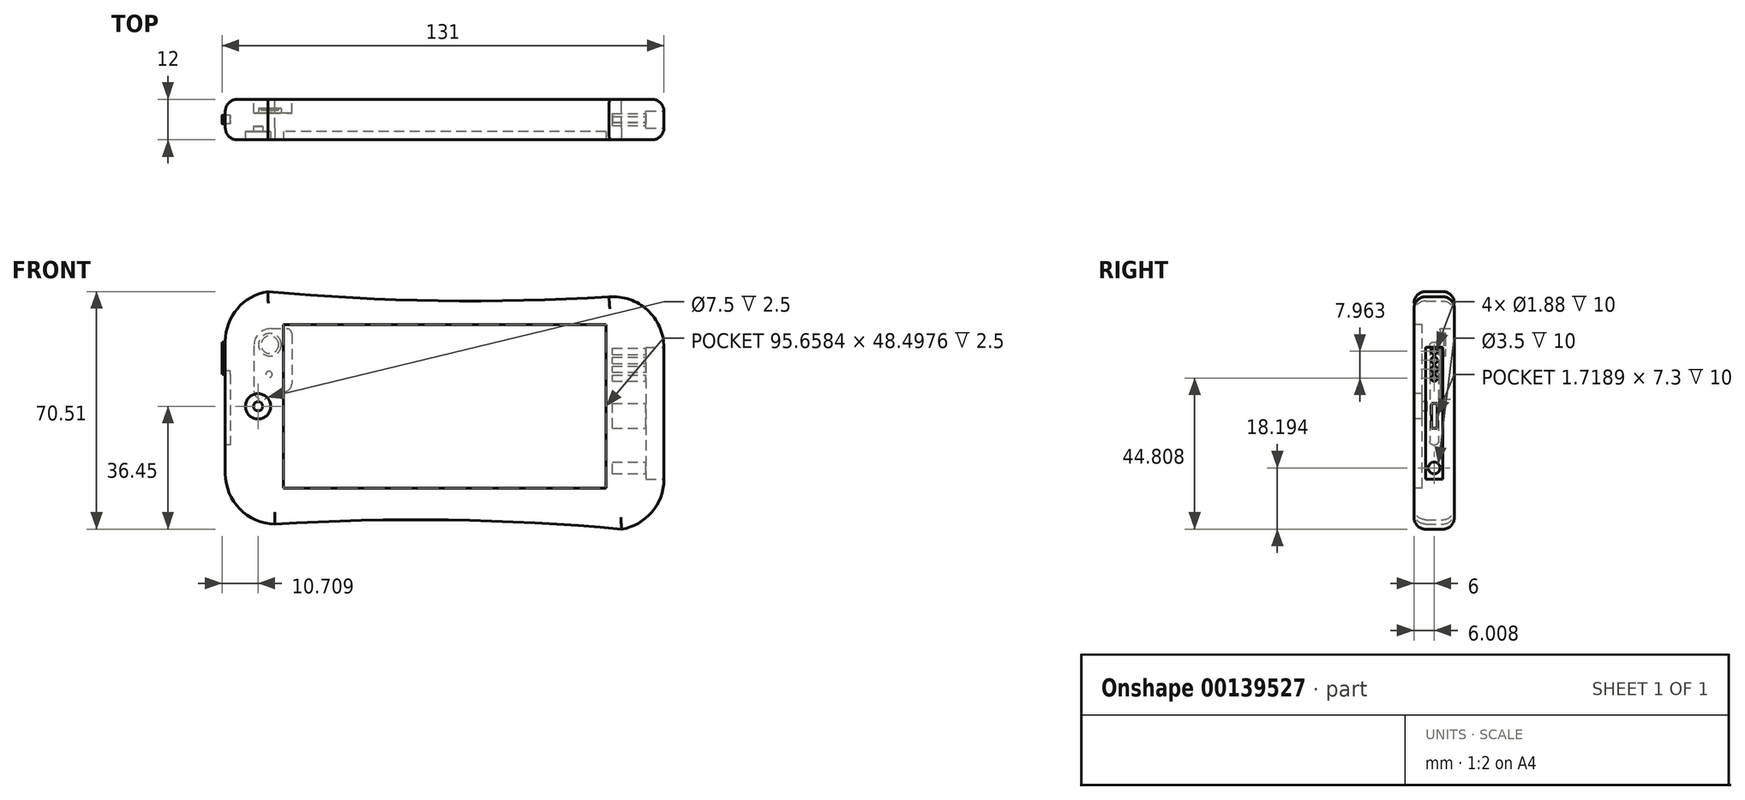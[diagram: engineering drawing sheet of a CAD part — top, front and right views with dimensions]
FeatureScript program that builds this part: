
annotation { "Feature Type Name" : "Feature", "Feature Type Description" : "" }
export const myFeature = defineFeature(function(context is Context, id is Id, definition is map)
    precondition{}
    {
        {
            var Q0;
            Q0=qCreatedBy(makeId("Front.planeOp"),FACE);
            var sketch = newSketch(context, id + "F0", { "sketchPlane" : qUnion([Q0])});
            skLineSegment(sketch, "E0.left", {"start": v(65, 17.5) * mm, "end": v(65, -21.65) * mm});
            skLineSegment(sketch, "E0.right", {"start": v(-65, 19.26) * mm, "end": v(-65, -19.94) * mm});
            skPoint(sketch, "E0.middle", {"position": v(0, 0) * mm});
            skPoint(sketch, "E1.visualSharp", {"position": v(-65, 3) * mm});
            skArc(sketch, "E1.filletArc", {"start": v(-52.42, 34.06) * mm, "mid": v(-61.43, 28.97) * mm, "end": v(-65, 19.26) * mm});
            skPoint(sketch, "E2.visualSharp", {"position": v(-65, -65) * mm});
            skArc(sketch, "E2.filletArc", {"start": v(-65, -19.94) * mm, "mid": v(-60.72, -30.44) * mm, "end": v(-50.32, -34.94) * mm});
            skPoint(sketch, "E3.visualSharp", {"position": v(65, 65) * mm});
            skArc(sketch, "E3.filletArc", {"start": v(65, 17.5) * mm, "mid": v(60.14, 28.56) * mm, "end": v(48.7, 32.45) * mm});
            skPoint(sketch, "E4.visualSharp", {"position": v(65, -3) * mm});
            skArc(sketch, "E4.filletArc", {"start": v(52.42, -36.45) * mm, "mid": v(61.43, -31.36) * mm, "end": v(65, -21.65) * mm});
            skArc(sketch, "E5", {"start": v(-52.42, 34.06) * mm, "mid": v(-1.89, 31.33) * mm, "end": v(48.7, 32.45) * mm});
            skArc(sketch, "E6", {"start": v(52.42, -36.45) * mm, "mid": v(1.07, -33.71) * mm, "end": v(-50.32, -34.94) * mm});
            skPoint(sketch, "E7", {"position": v(-45, 23.39) * mm});
            skPoint(sketch, "E8", {"position": v(45, 22.22) * mm});
            skPoint(sketch, "E9", {"position": v(45, -25.78) * mm});
            skPoint(sketch, "E10", {"position": v(-45, -24.61) * mm});
            skLineSegment(sketch, "E11", {"start": v(-45, 23.39) * mm, "end": v(-45, -24.61) * mm});
            skLineSegment(sketch, "E12", {"start": v(45, -25.78) * mm, "end": v(-45, -24.61) * mm});
            skLineSegment(sketch, "E13", {"start": v(45, -25.78) * mm, "end": v(45, 22.22) * mm});
            skLineSegment(sketch, "E14", {"start": v(45, 22.22) * mm, "end": v(-45, 23.39) * mm});
            skSolve(sketch);
        }
        {
            var Q0;
            Q0=makeQuery(id+"F0.imprint","IMPRINT",FACE,{"disambiguationData":[TD([[makeQuery(id+"F0.imprint","IMPRINT",EDGE,{"derivedFrom":sQuery(id+"F0.wireOp",EDGE,"E11")}),1.0]])]});
            var Q1;
            Q1=makeQuery(id+"F0.imprint","IMPRINT",FACE,{"disambiguationData":[TD([[makeQuery(id+"F0.imprint","IMPRINT",EDGE,{"derivedFrom":sQuery(id+"F0.wireOp",EDGE,"E0.left")}),-1.0]])]});
            extrude(context, id + "F1", {"entities" : qUnion([Q0, Q1]), "depth" : 12 * mm});
        }
        {
            var Q0;
            Q0=makeQuery(id+"F1.opExtrude","CAP_FACE",FACE,{"disambiguationData":[OSD([sQuery(id+"F0.wireOp",EDGE,"E0.left"),sQuery(id+"F0.wireOp",EDGE,"E0.right"),sQuery(id+"F0.wireOp",EDGE,"E1.filletArc"),sQuery(id+"F0.wireOp",EDGE,"E2.filletArc"),sQuery(id+"F0.wireOp",EDGE,"E3.filletArc"),sQuery(id+"F0.wireOp",EDGE,"E4.filletArc"),sQuery(id+"F0.wireOp",EDGE,"E5"),sQuery(id+"F0.wireOp",EDGE,"E6")])],"isStart":false});
            fillet(context, id + "F2", {"entities" : qUnion([Q0]), "radius" : 3.5 * mm, "tangentPropagation" : true, "allowEdgeOverflow" : false});
        }
        {
            var Q0;
            Q0=makeQuery(id+"F1.opExtrude","CAP_FACE",FACE,{"disambiguationData":[OSD([sQuery(id+"F0.wireOp",EDGE,"E0.left"),sQuery(id+"F0.wireOp",EDGE,"E0.right"),sQuery(id+"F0.wireOp",EDGE,"E1.filletArc"),sQuery(id+"F0.wireOp",EDGE,"E2.filletArc"),sQuery(id+"F0.wireOp",EDGE,"E3.filletArc"),sQuery(id+"F0.wireOp",EDGE,"E4.filletArc"),sQuery(id+"F0.wireOp",EDGE,"E5"),sQuery(id+"F0.wireOp",EDGE,"E6")])],"isStart":true});
            fillet(context, id + "F3", {"entities" : qUnion([Q0]), "radius" : 3.5 * mm, "tangentPropagation" : true, "allowEdgeOverflow" : false});
        }
        {
            var Q0;
            Q0=makeQuery(id+"F1.opExtrude","CAP_FACE",FACE,{"disambiguationData":[OSD([sQuery(id+"F0.wireOp",EDGE,"E0.left"),sQuery(id+"F0.wireOp",EDGE,"E0.right"),sQuery(id+"F0.wireOp",EDGE,"E1.filletArc"),sQuery(id+"F0.wireOp",EDGE,"E2.filletArc"),sQuery(id+"F0.wireOp",EDGE,"E3.filletArc"),sQuery(id+"F0.wireOp",EDGE,"E4.filletArc"),sQuery(id+"F0.wireOp",EDGE,"E5"),sQuery(id+"F0.wireOp",EDGE,"E6")])],"isStart":false});
            var sketch = newSketch(context, id + "F4", { "sketchPlane" : qUnion([Q0])});
            skLineSegment(sketch, "E15.bottom", {"start": v(47.83, -24.25) * mm, "end": v(-47.83, -24.25) * mm});
            skLineSegment(sketch, "E15.top", {"start": v(47.83, 24.25) * mm, "end": v(-47.83, 24.25) * mm});
            skLineSegment(sketch, "E15.left", {"start": v(47.83, -24.25) * mm, "end": v(47.83, 24.25) * mm});
            skLineSegment(sketch, "E15.right", {"start": v(-47.83, -24.25) * mm, "end": v(-47.83, 24.25) * mm});
            skPoint(sketch, "E15.middle", {"position": v(0, 0) * mm});
            skCircle(sketch, "E16", {"center": v(-55.3, 0) * mm, "radius": 3.75 * mm});
            skSolve(sketch);
        }
        {
            var Q0;
            Q0 = qSketchRegion(id + "F4", true);
            extrude(context, id + "F5", {"entities" : qUnion([Q0]), "operationType" : NewBodyOperationType.REMOVE, "oppositeDirection" : true, "depth" : 2.5 * mm});
        }
        {
            var Q0;
            Q0=makeQuery(id+"F5.boolean.opBoolean","COPY",FACE,{"derivedFrom":makeQuery(id+"F5.opExtrude","CAP_FACE",FACE,{"disambiguationData":[OSD([sQuery(id+"F4.wireOp",EDGE,"E16")])],"isStart":false})});
            var sketch = newSketch(context, id + "F6", { "sketchPlane" : qUnion([Q0])});
            skCircle(sketch, "E17", {"center": v(-55.3, 0) * mm, "radius": 1.37 * mm});
            skSolve(sketch);
        }
        {
            var Q0;
            Q0 = qSketchRegion(id + "F6", true);
            extrude(context, id + "F7", {"entities" : qUnion([Q0]), "operationType" : NewBodyOperationType.REMOVE, "oppositeDirection" : true, "depth" : 1.5 * mm});
        }
        {
            var Q0;
            Q0=makeQuery(id+"F1.opExtrude","SWEPT_FACE",FACE,{"disambiguationData":[OSD([sQuery(id+"F0.wireOp",EDGE,"E0.left")])]});
            var sketch = newSketch(context, id + "F8", { "sketchPlane" : qUnion([Q0])});
            skSolve(sketch);
        }
        {
            var Q0;
            {var subQ0=sQuery(id+"F0.wireOp",EDGE,"E0.left");var subQ1=makeQuery(id+"F1.opExtrude","SWEPT_FACE",FACE,{"disambiguationData":[OSD([subQ0])]});Q0=makeQuery(id+"F8.imprint","IMPRINT",FACE,{"disambiguationData":[TD([[makeQuery(id+"F8.imprint","IMPRINT",EDGE,{"derivedFrom":makeQuery(id+"F2.opFillet","BLEND_EDGE",EDGE,{"blendedFrom":[makeQuery(id+"F1.opExtrude","CAP_EDGE",EDGE,{"disambiguationData":[OSD([subQ0])],"isStart":false}),subQ1],"blendedInto":[subQ1]})}),1.0]])]});}
            extrude(context, id + "F9", {"entities" : qUnion([Q0]), "operationType" : NewBodyOperationType.REMOVE, "oppositeDirection" : true, "depth" : 5.3 * mm});
        }
        {
            var Q0;
            Q0=makeQuery(id+"F9.boolean.opBoolean","COPY",FACE,{"derivedFrom":makeQuery(id+"F9.opExtrude","CAP_FACE",FACE,{"disambiguationData":[OSD([sQuery(id+"F0.wireOp",EDGE,"E0.left"),sQuery(id+"F0.wireOp",EDGE,"E3.filletArc"),sQuery(id+"F0.wireOp",EDGE,"E4.filletArc")])],"isStart":false})});
            var sketch = newSketch(context, id + "F10", { "sketchPlane" : qUnion([Q0])});
            skCircle(sketch, "E18", {"center": v(-6, -18.25) * mm, "radius": 1.75 * mm});
            skPoint(sketch, "E18.centerSnap0", {"position": v(-6, -21.65) * mm});
            skLineSegment(sketch, "E19.bottom", {"start": v(-6.77, -6.49) * mm, "end": v(-5.05, -6.49) * mm});
            skLineSegment(sketch, "E19.top", {"start": v(-6.77, 0.81) * mm, "end": v(-5.05, 0.81) * mm});
            skLineSegment(sketch, "E19.left", {"start": v(-6.77, -6.49) * mm, "end": v(-6.77, 0.81) * mm});
            skLineSegment(sketch, "E19.right", {"start": v(-5.05, -6.49) * mm, "end": v(-5.05, 0.81) * mm});
            skCircle(sketch, "E20", {"center": v(-6, 8.36) * mm, "radius": 0.94 * mm});
            skCircle(sketch, "E21.0.1.0", {"center": v(-6, 11.01) * mm, "radius": 0.94 * mm});
            skCircle(sketch, "E21.0.2.0", {"center": v(-6, 13.67) * mm, "radius": 0.94 * mm});
            skCircle(sketch, "E21.0.3.0", {"center": v(-6, 16.32) * mm, "radius": 0.94 * mm});
            skLineSegment(sketch, "E21.direction1", {"start": v(-6, 8.36) * mm, "end": v(19, 8.36) * mm, "construction": true});
            skLineSegment(sketch, "E21.direction2", {"start": v(-6, 8.36) * mm, "end": v(-6, 11.01) * mm, "construction": true});
            skSolve(sketch);
        }
        {
            var Q0;
            Q0 = qSketchRegion(id + "F10", true);
            extrude(context, id + "F11", {"entities" : qUnion([Q0]), "operationType" : NewBodyOperationType.REMOVE, "oppositeDirection" : true, "depth" : 10 * mm});
        }
        {
            var Q0;
            Q0=makeQuery(id+"F1.opExtrude","CAP_FACE",FACE,{"disambiguationData":[OSD([sQuery(id+"F0.wireOp",EDGE,"E0.left"),sQuery(id+"F0.wireOp",EDGE,"E0.right"),sQuery(id+"F0.wireOp",EDGE,"E1.filletArc"),sQuery(id+"F0.wireOp",EDGE,"E2.filletArc"),sQuery(id+"F0.wireOp",EDGE,"E3.filletArc"),sQuery(id+"F0.wireOp",EDGE,"E4.filletArc"),sQuery(id+"F0.wireOp",EDGE,"E5"),sQuery(id+"F0.wireOp",EDGE,"E6")])],"isStart":true});
            var sketch = newSketch(context, id + "F12", { "sketchPlane" : qUnion([Q0])});
            skLineSegment(sketch, "E22.bottom", {"start": v(51.5, 23.03) * mm, "end": v(46.78, 23.03) * mm});
            skLineSegment(sketch, "E22.left", {"start": v(56.5, 18.03) * mm, "end": v(56.5, 4.58) * mm});
            skLineSegment(sketch, "E22.right", {"start": v(45.28, 21.53) * mm, "end": v(45.28, 6.8) * mm});
            skLineSegment(sketch, "E23", {"start": v(46.94, 4.44) * mm, "end": v(53.16, 2.22) * mm});
            skPoint(sketch, "E24.visualSharp", {"position": v(45.28, 5.03) * mm});
            skArc(sketch, "E24.filletArc", {"start": v(45.28, 6.8) * mm, "mid": v(45.74, 5.35) * mm, "end": v(46.94, 4.44) * mm});
            skPoint(sketch, "E25.visualSharp", {"position": v(56.5, 1.03) * mm});
            skArc(sketch, "E25.filletArc", {"start": v(53.16, 2.22) * mm, "mid": v(55.44, 2.53) * mm, "end": v(56.5, 4.58) * mm});
            skPoint(sketch, "E26.visualSharp", {"position": v(56.5, 23.03) * mm});
            skArc(sketch, "E26.filletArc", {"start": v(56.5, 18.03) * mm, "mid": v(55.03, 21.57) * mm, "end": v(51.5, 23.03) * mm});
            skPoint(sketch, "E27.visualSharp", {"position": v(45.28, 23.03) * mm});
            skArc(sketch, "E27.filletArc", {"start": v(46.78, 23.03) * mm, "mid": v(45.72, 22.6) * mm, "end": v(45.28, 21.53) * mm});
            skSolve(sketch);
        }
        {
            var Q0;
            Q0 = qSketchRegion(id + "F12", true);
            extrude(context, id + "F13", {"entities" : qUnion([Q0]), "operationType" : NewBodyOperationType.REMOVE, "oppositeDirection" : true, "depth" : 4.15 * mm});
        }
        {
            var Q0;
            Q0=makeQuery(id+"F13.boolean.opBoolean","COPY",FACE,{"derivedFrom":makeQuery(id+"F13.opExtrude","CAP_FACE",FACE,{"disambiguationData":[OSD([sQuery(id+"F12.wireOp",EDGE,"E22.bottom"),sQuery(id+"F12.wireOp",EDGE,"E22.left"),sQuery(id+"F12.wireOp",EDGE,"E22.right"),sQuery(id+"F12.wireOp",EDGE,"E23"),sQuery(id+"F12.wireOp",EDGE,"E24.filletArc"),sQuery(id+"F12.wireOp",EDGE,"E25.filletArc"),sQuery(id+"F12.wireOp",EDGE,"E26.filletArc"),sQuery(id+"F12.wireOp",EDGE,"E27.filletArc")])],"isStart":false})});
            var sketch = newSketch(context, id + "F14", { "sketchPlane" : qUnion([Q0])});
            skCircle(sketch, "E28", {"center": v(51.8, 18.26) * mm, "radius": 3.37 * mm});
            skCircle(sketch, "E29", {"center": v(52.06, 9.46) * mm, "radius": 0.94 * mm});
            skSolve(sketch);
        }
        {
            var Q0;
            Q0 = qSketchRegion(id + "F14", true);
            extrude(context, id + "F15", {"entities" : qUnion([Q0]), "operationType" : NewBodyOperationType.ADD, "depth" : 1.5 * mm});
        }
        {
            var Q0;
            Q0=makeQuery(id+"F15.opExtrude","CAP_FACE",FACE,{"disambiguationData":[OSD([sQuery(id+"F14.wireOp",EDGE,"E28")])],"isStart":false});
            var sketch = newSketch(context, id + "F16", { "sketchPlane" : qUnion([Q0])});
            skCircle(sketch, "E30", {"center": v(51.8, 18.26) * mm, "radius": 2.6 * mm});
            skSolve(sketch);
        }
        {
            var Q0;
            Q0 = qSketchRegion(id + "F16", true);
            extrude(context, id + "F17", {"entities" : qUnion([Q0]), "operationType" : NewBodyOperationType.REMOVE, "oppositeDirection" : true, "depth" : .5 * mm});
        }
        {
            var Q0;
            Q0=makeQuery(id+"F15.opExtrude","CAP_FACE",FACE,{"disambiguationData":[OSD([sQuery(id+"F14.wireOp",EDGE,"E29")])],"isStart":false});
            var sketch = newSketch(context, id + "F18", { "sketchPlane" : qUnion([Q0])});
            skCircle(sketch, "E31", {"center": v(52.06, 9.46) * mm, "radius": 1.1 * mm});
            skSolve(sketch);
        }
        {
            var Q0;
            Q0 = qSketchRegion(id + "F18", true);
            extrude(context, id + "F19", {"entities" : qUnion([Q0]), "operationType" : NewBodyOperationType.REMOVE, "oppositeDirection" : true, "depth" : 1.25 * mm});
        }
        {
            var Q0;
            Q0 = qSketchRegion(id + "F18", true);
            extrude(context, id + "F20", {"entities" : qUnion([Q0]), "operationType" : NewBodyOperationType.REMOVE, "oppositeDirection" : true, "depth" : 0.15 * mm});
        }
        {
            var Q0;
            Q0=makeQuery(id+"F1.opExtrude","SWEPT_FACE",FACE,{"disambiguationData":[OSD([sQuery(id+"F0.wireOp",EDGE,"E0.right")])]});
            var sketch = newSketch(context, id + "F21", { "sketchPlane" : qUnion([Q0])});
            skLineSegment(sketch, "E32.bottom", {"start": v(6.25, 19.06) * mm, "end": v(5.75, 19.06) * mm});
            skLineSegment(sketch, "E32.top", {"start": v(6.25, 9.56) * mm, "end": v(5.75, 9.56) * mm});
            skLineSegment(sketch, "E32.left", {"start": v(7.25, 18.06) * mm, "end": v(7.25, 10.56) * mm});
            skLineSegment(sketch, "E32.right", {"start": v(4.75, 18.06) * mm, "end": v(4.75, 10.56) * mm});
            skPoint(sketch, "E33.visualSharp", {"position": v(7.25, 9.56) * mm});
            skArc(sketch, "E33.filletArc", {"start": v(6.25, 9.56) * mm, "mid": v(6.96, 9.85) * mm, "end": v(7.25, 10.56) * mm});
            skPoint(sketch, "E34.visualSharp", {"position": v(4.75, 9.56) * mm});
            skArc(sketch, "E34.filletArc", {"start": v(4.75, 10.56) * mm, "mid": v(5.05, 9.85) * mm, "end": v(5.75, 9.56) * mm});
            skPoint(sketch, "E35.visualSharp", {"position": v(4.75, 19.06) * mm});
            skArc(sketch, "E35.filletArc", {"start": v(5.75, 19.06) * mm, "mid": v(5.05, 18.77) * mm, "end": v(4.75, 18.06) * mm});
            skPoint(sketch, "E36.visualSharp", {"position": v(7.25, 19.06) * mm});
            skArc(sketch, "E36.filletArc", {"start": v(7.25, 18.06) * mm, "mid": v(6.96, 18.77) * mm, "end": v(6.25, 19.06) * mm});
            skSolve(sketch);
        }
        {
            var Q0;
            Q0 = qSketchRegion(id + "F21", true);
            extrude(context, id + "F22", {"entities" : qUnion([Q0]), "operationType" : NewBodyOperationType.ADD, "depth" : 1 * mm});
        }
        {
            var Q0;
            Q0=makeQuery(id+"F1.opExtrude","SWEPT_FACE",FACE,{"disambiguationData":[OSD([sQuery(id+"F0.wireOp",EDGE,"E0.right")])]});
            var sketch = newSketch(context, id + "F23", { "sketchPlane" : qUnion([Q0])});
            skLineSegment(sketch, "E37.bottom", {"start": v(6.25, 10.56) * mm, "end": v(5.75, 10.56) * mm});
            skLineSegment(sketch, "E37.top", {"start": v(6.25, -11.45) * mm, "end": v(5.75, -11.45) * mm});
            skLineSegment(sketch, "E37.left", {"start": v(7.25, 9.56) * mm, "end": v(7.25, -10.45) * mm});
            skLineSegment(sketch, "E37.right", {"start": v(4.75, 9.56) * mm, "end": v(4.75, -10.45) * mm});
            skPoint(sketch, "E38.visualSharp", {"position": v(7.25, 10.56) * mm});
            skArc(sketch, "E38.filletArc", {"start": v(7.25, 9.56) * mm, "mid": v(6.96, 10.27) * mm, "end": v(6.25, 10.56) * mm});
            skPoint(sketch, "E39.visualSharp", {"position": v(7.25, -11.45) * mm});
            skArc(sketch, "E39.filletArc", {"start": v(6.25, -11.45) * mm, "mid": v(6.96, -11.16) * mm, "end": v(7.25, -10.45) * mm});
            skPoint(sketch, "E40.visualSharp", {"position": v(4.75, -11.45) * mm});
            skArc(sketch, "E40.filletArc", {"start": v(4.75, -10.45) * mm, "mid": v(5.05, -11.16) * mm, "end": v(5.75, -11.45) * mm});
            skPoint(sketch, "E41.visualSharp", {"position": v(4.75, 10.56) * mm});
            skArc(sketch, "E41.filletArc", {"start": v(5.75, 10.56) * mm, "mid": v(5.05, 10.27) * mm, "end": v(4.75, 9.56) * mm});
            skSolve(sketch);
        }
        {
            var Q0;
            Q0 = qSketchRegion(id + "F23", true);
            extrude(context, id + "F24", {"entities" : qUnion([Q0]), "operationType" : NewBodyOperationType.REMOVE, "oppositeDirection" : true, "depth" : 1.5 * mm});
        }
    });
